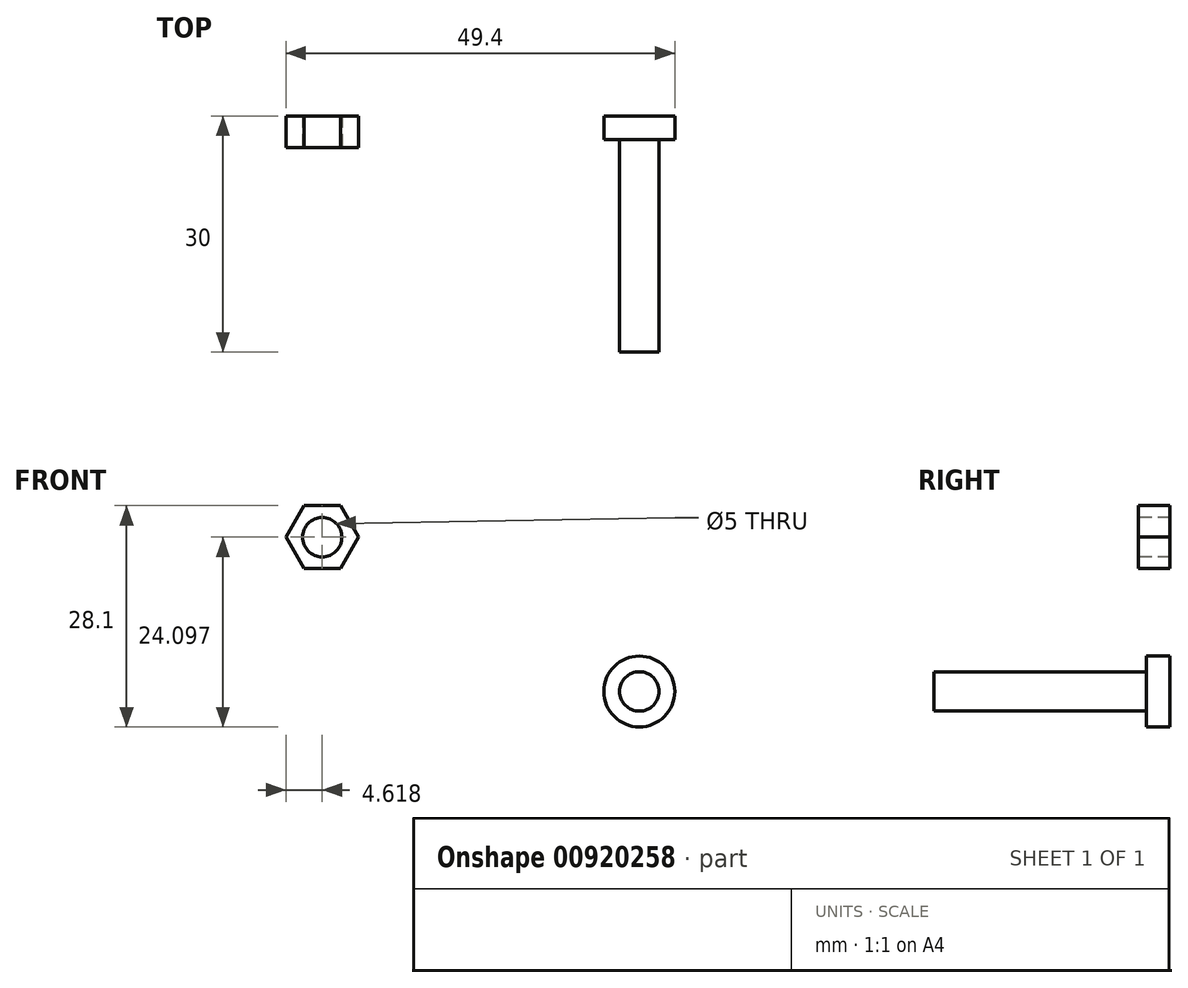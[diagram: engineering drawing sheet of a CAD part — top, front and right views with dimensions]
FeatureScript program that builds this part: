
annotation { "Feature Type Name" : "Feature", "Feature Type Description" : "" }
export const myFeature = defineFeature(function(context is Context, id is Id, definition is map)
    precondition{}
    {
        {
            var Q0;
            Q0=qCreatedBy(makeId("Front.planeOp"),FACE);
            var sketch = newSketch(context, id + "F0", { "sketchPlane" : qUnion([Q0])});
            skCircle(sketch, "E0", {"center": v(0, 0) * mm, "radius": 4.5 * mm});
            skSolve(sketch);
        }
        {
            var Q0;
            Q0 = qSketchRegion(id + "F0", true);
            extrude(context, id + "F1", {"entities" : qUnion([Q0]), "depth" : 3 * mm, "offsetDistance" : 25 * mm});
        }
        {
            var Q0;
            Q0=makeQuery(id+"F1.opExtrude","CAP_FACE",FACE,{"disambiguationData":[OSD([sQuery(id+"F0.wireOp",EDGE,"E0")])],"isStart":false});
            var sketch = newSketch(context, id + "F2", { "sketchPlane" : qUnion([Q0])});
            skCircle(sketch, "E1", {"center": v(0, 0) * mm, "radius": 2.5 * mm});
            skSolve(sketch);
        }
        {
            var Q0;
            Q0 = qSketchRegion(id + "F2", true);
            extrude(context, id + "F3", {"entities" : qUnion([Q0]), "depth" : 27 * mm, "offsetDistance" : 25 * mm});
        }
        {
            var Q0;
            Q0=qCreatedBy(makeId("Front.planeOp"),FACE);
            var sketch = newSketch(context, id + "F4", { "sketchPlane" : qUnion([Q0])});
            skCircle(sketch, "E2.cCircle", {"center": v(-40.28, 19.6) * mm, "radius": 4 * mm, "construction": true});
            skLineSegment(sketch, "E2.0", {"start": v(-37.97, 15.6) * mm, "end": v(-42.6, 15.6) * mm});
            skLineSegment(sketch, "E2.1", {"start": v(-42.6, 15.6) * mm, "end": v(-44.9, 19.6) * mm});
            skLineSegment(sketch, "E2.2", {"start": v(-44.9, 19.6) * mm, "end": v(-42.6, 23.6) * mm});
            skLineSegment(sketch, "E2.3", {"start": v(-42.6, 23.6) * mm, "end": v(-37.97, 23.6) * mm});
            skLineSegment(sketch, "E2.4", {"start": v(-37.97, 23.6) * mm, "end": v(-35.66, 19.6) * mm});
            skLineSegment(sketch, "E2.5", {"start": v(-35.66, 19.6) * mm, "end": v(-37.97, 15.6) * mm});
            skPoint(sketch, "E2.0.midPoint", {"position": v(-40.28, 15.6) * mm});
            skSolve(sketch);
        }
        {
            var Q0;
            Q0 = qSketchRegion(id + "F4", true);
            extrude(context, id + "F5", {"entities" : qUnion([Q0]), "depth" : 4 * mm, "offsetDistance" : 25 * mm});
        }
        {
            var Q0;
            Q0=makeQuery(id+"F5.opExtrude","CAP_FACE",FACE,{"disambiguationData":[OSD([sQuery(id+"F4.wireOp",EDGE,"E2.0"),sQuery(id+"F4.wireOp",EDGE,"E2.1"),sQuery(id+"F4.wireOp",EDGE,"E2.2"),sQuery(id+"F4.wireOp",EDGE,"E2.3"),sQuery(id+"F4.wireOp",EDGE,"E2.4"),sQuery(id+"F4.wireOp",EDGE,"E2.5")])],"isStart":false});
            var sketch = newSketch(context, id + "F6", { "sketchPlane" : qUnion([Q0])});
            skCircle(sketch, "E3", {"center": v(-40.28, 19.6) * mm, "radius": 2.5 * mm});
            skPoint(sketch, "E3.centerSnap0", {"position": v(-40.28, 23.6) * mm});
            skSolve(sketch);
        }
        {
            var Q0;
            Q0 = qSketchRegion(id + "F6", true);
            extrude(context, id + "F7", {"entities" : qUnion([Q0]), "operationType" : NewBodyOperationType.REMOVE, "endBound" : BoundingType.UP_TO_NEXT, "oppositeDirection" : true, "depth" : 25 * mm, "offsetDistance" : 25 * mm});
        }
    });
